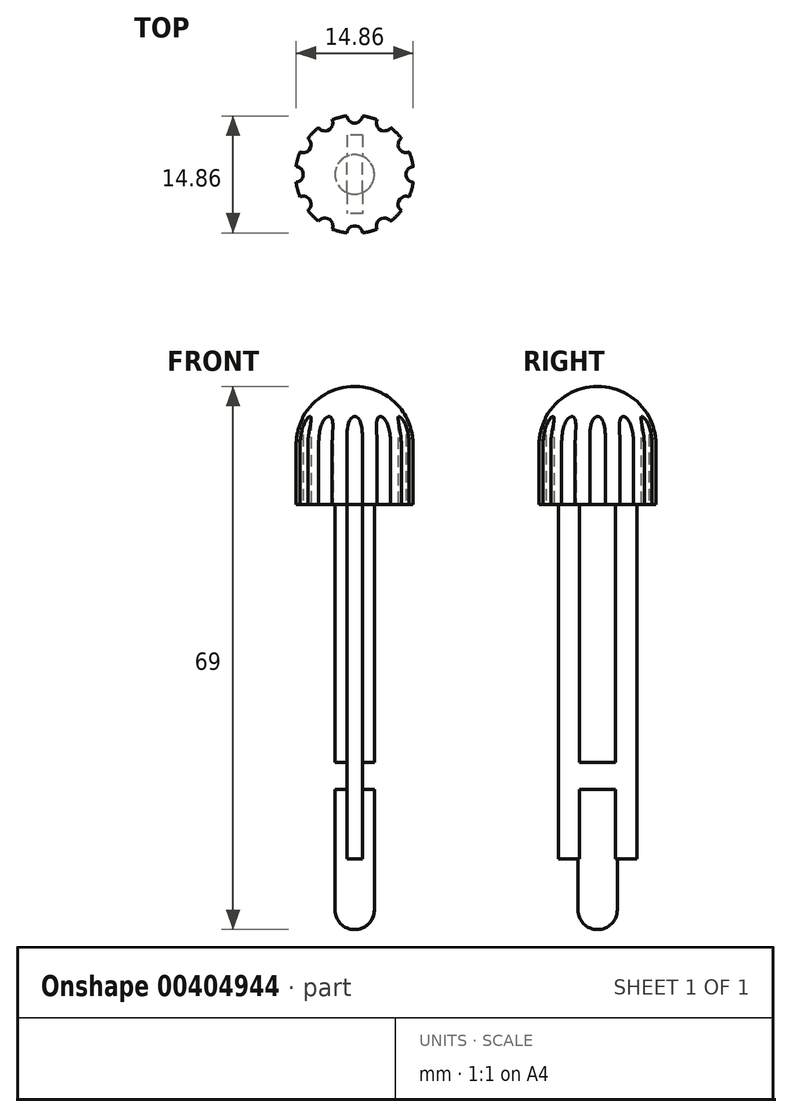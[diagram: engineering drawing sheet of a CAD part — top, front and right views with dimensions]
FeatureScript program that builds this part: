
annotation { "Feature Type Name" : "Feature", "Feature Type Description" : "" }
export const myFeature = defineFeature(function(context is Context, id is Id, definition is map)
    precondition{}
    {
        {
            var Q0;
            Q0=qCreatedBy(makeId("Top.planeOp"),FACE);
            var sketch = newSketch(context, id + "F0", { "sketchPlane" : qUnion([Q0])});
            skCircle(sketch, "E0", {"center": v(0, 0) * mm, "radius": 7.5 * mm});
            skCircle(sketch, "E1", {"center": v(0, 0) * mm, "radius": 2.5 * mm});
            skLineSegment(sketch, "E2.bottom", {"start": v(1, 5) * mm, "end": v(-1, 5) * mm});
            skLineSegment(sketch, "E2.top", {"start": v(1, -5) * mm, "end": v(-1, -5) * mm});
            skLineSegment(sketch, "E2.left", {"start": v(1, 5) * mm, "end": v(1, -5) * mm});
            skLineSegment(sketch, "E2.right", {"start": v(-1, 5) * mm, "end": v(-1, -5) * mm});
            skSolve(sketch);
        }
        {
            var Q0;
            Q0 = qSketchRegion(id + "F0", true);
            var Q1;
            {var subQ0=sQuery(id+"F0.wireOp",EDGE,"E2.left");var subQ1=sQuery(id+"F0.wireOp",EDGE,"E1");var subQ2=makeQuery(id+"F0.imprint","INTERSECT",VERTEX,{"disambiguationData":[OD(0.0)],"derivedFrom":[subQ1,subQ0]});Q1=makeQuery(id+"F0.imprint","IMPRINT",FACE,{"disambiguationData":[TD([[makeQuery(id+"F0.imprint","IMPRINT",EDGE,{"disambiguationData":[TD([[subQ2,1.0]])],"derivedFrom":subQ1}),1.0]])]});}
            var Q2;
            {var subQ0=sQuery(id+"F0.wireOp",EDGE,"E2.right");var subQ1=sQuery(id+"F0.wireOp",EDGE,"E1");var subQ2=makeQuery(id+"F0.imprint","INTERSECT",VERTEX,{"disambiguationData":[OD(0.0)],"derivedFrom":[subQ1,subQ0]});Q2=makeQuery(id+"F0.imprint","IMPRINT",FACE,{"disambiguationData":[TD([[makeQuery(id+"F0.imprint","IMPRINT",EDGE,{"disambiguationData":[TD([[subQ2,-1.0]])],"derivedFrom":subQ1}),1.0]])]});}
            var Q3;
            {var subQ0=sQuery(id+"F0.wireOp",EDGE,"E2.right");var subQ1=sQuery(id+"F0.wireOp",EDGE,"E1");var subQ2=makeQuery(id+"F0.imprint","INTERSECT",VERTEX,{"disambiguationData":[OD(0.0)],"derivedFrom":[subQ1,subQ0]});Q3=makeQuery(id+"F0.imprint","IMPRINT",FACE,{"disambiguationData":[TD([[makeQuery(id+"F0.imprint","IMPRINT",EDGE,{"disambiguationData":[TD([[subQ2,1.0]])],"derivedFrom":subQ1}),1.0]])]});}
            var Q4;
            {var subQ5=sQuery(id+"F0.wireOp",EDGE,"E2.bottom");Q4=makeQuery(id+"F0.imprint","IMPRINT",FACE,{"disambiguationData":[TD([[makeQuery(id+"F0.imprint","IMPRINT",EDGE,{"derivedFrom":subQ5}),1.0]])]});}
            var Q5;
            {var subQ5=sQuery(id+"F0.wireOp",EDGE,"E2.top");Q5=makeQuery(id+"F0.imprint","IMPRINT",FACE,{"disambiguationData":[TD([[makeQuery(id+"F0.imprint","IMPRINT",EDGE,{"derivedFrom":subQ5}),-1.0]])]});}
            extrude(context, id + "F1", {"entities" : qUnion([Q0, Q1, Q2, Q3, Q4, Q5]), "depth" : 15 * mm});
        }
        {
            var Q0;
            {var subQ0=sQuery(id+"F0.wireOp",EDGE,"E2.right");var subQ1=sQuery(id+"F0.wireOp",EDGE,"E1");var subQ2=makeQuery(id+"F0.imprint","INTERSECT",VERTEX,{"disambiguationData":[OD(0.0)],"derivedFrom":[subQ1,subQ0]});Q0=makeQuery(id+"F0.imprint","IMPRINT",FACE,{"disambiguationData":[TD([[makeQuery(id+"F0.imprint","IMPRINT",EDGE,{"disambiguationData":[TD([[subQ2,1.0]])],"derivedFrom":subQ1}),1.0]])]});}
            var Q1;
            {var subQ0=sQuery(id+"F0.wireOp",EDGE,"E2.right");var subQ1=sQuery(id+"F0.wireOp",EDGE,"E1");var subQ2=makeQuery(id+"F0.imprint","INTERSECT",VERTEX,{"disambiguationData":[OD(0.0)],"derivedFrom":[subQ1,subQ0]});Q1=makeQuery(id+"F0.imprint","IMPRINT",FACE,{"disambiguationData":[TD([[makeQuery(id+"F0.imprint","IMPRINT",EDGE,{"disambiguationData":[TD([[subQ2,-1.0]])],"derivedFrom":subQ1}),1.0]])]});}
            var Q2;
            {var subQ0=sQuery(id+"F0.wireOp",EDGE,"E2.left");var subQ1=sQuery(id+"F0.wireOp",EDGE,"E1");var subQ2=makeQuery(id+"F0.imprint","INTERSECT",VERTEX,{"disambiguationData":[OD(0.0)],"derivedFrom":[subQ1,subQ0]});Q2=makeQuery(id+"F0.imprint","IMPRINT",FACE,{"disambiguationData":[TD([[makeQuery(id+"F0.imprint","IMPRINT",EDGE,{"disambiguationData":[TD([[subQ2,1.0]])],"derivedFrom":subQ1}),1.0]])]});}
            extrude(context, id + "F2", {"entities" : qUnion([Q0, Q1, Q2]), "operationType" : NewBodyOperationType.ADD, "oppositeDirection" : true, "depth" : 54 * mm});
        }
        {
            var Q0;
            {var subQ5=sQuery(id+"F0.wireOp",EDGE,"E2.bottom");Q0=makeQuery(id+"F0.imprint","IMPRINT",FACE,{"disambiguationData":[TD([[makeQuery(id+"F0.imprint","IMPRINT",EDGE,{"derivedFrom":subQ5}),1.0]])]});}
            var Q1;
            {var subQ5=sQuery(id+"F0.wireOp",EDGE,"E2.top");Q1=makeQuery(id+"F0.imprint","IMPRINT",FACE,{"disambiguationData":[TD([[makeQuery(id+"F0.imprint","IMPRINT",EDGE,{"derivedFrom":subQ5}),-1.0]])]});}
            extrude(context, id + "F3", {"entities" : qUnion([Q0, Q1]), "operationType" : NewBodyOperationType.ADD, "oppositeDirection" : true, "depth" : 45 * mm});
        }
        {
            var Q0;
            Q0=makeQuery(id+"F2.opExtrude","CAP_FACE",FACE,{"disambiguationData":[OSD([sQuery(id+"F0.wireOp",EDGE,"E1")])],"isStart":false});
            fillet(context, id + "F4", {"entities" : qUnion([Q0]), "radius" : 2.5 * mm, "tangentPropagation" : true, "allowEdgeOverflow" : false});
        }
        {
            var Q0;
            Q0=makeQuery(id+"F1.opExtrude","CAP_FACE",FACE,{"disambiguationData":[OSD([sQuery(id+"F0.wireOp",EDGE,"E0")])],"isStart":false});
            fillet(context, id + "F5", {"entities" : qUnion([Q0]), "radius" : 7.5 * mm, "tangentPropagation" : true, "allowEdgeOverflow" : false});
        }
        {
            var Q0;
            Q0=makeQuery(id+"F3.opExtrude","SWEPT_FACE",FACE,{"disambiguationData":[OSD([sQuery(id+"F0.wireOp",EDGE,"E2.bottom")])]});
            var sketch = newSketch(context, id + "F6", { "sketchPlane" : qUnion([Q0])});
            skLineSegment(sketch, "E3.bottom", {"start": v(1, -32.74) * mm, "end": v(3.02, -32.74) * mm});
            skLineSegment(sketch, "E3.top", {"start": v(1, -36.22) * mm, "end": v(3.02, -36.22) * mm});
            skLineSegment(sketch, "E3.left", {"start": v(1, -32.74) * mm, "end": v(1, -36.22) * mm});
            skLineSegment(sketch, "E3.right", {"start": v(3.02, -32.74) * mm, "end": v(3.02, -36.22) * mm});
            skLineSegment(sketch, "E4.bottom", {"start": v(-1, -32.74) * mm, "end": v(-3.02, -32.74) * mm});
            skLineSegment(sketch, "E4.top", {"start": v(-1, -36.22) * mm, "end": v(-3.02, -36.22) * mm});
            skLineSegment(sketch, "E4.left", {"start": v(-1, -32.74) * mm, "end": v(-1, -36.22) * mm});
            skLineSegment(sketch, "E4.right", {"start": v(-3.02, -32.74) * mm, "end": v(-3.02, -36.22) * mm});
            skSolve(sketch);
        }
        {
            var Q0;
            Q0=makeQuery(id+"F6.imprint","IMPRINT",FACE,{"disambiguationData":[TD([[makeQuery(id+"F6.imprint","IMPRINT",EDGE,{"derivedFrom":sQuery(id+"F6.wireOp",EDGE,"E4.bottom")}),1.0]])]});
            var Q1;
            Q1=makeQuery(id+"F6.imprint","IMPRINT",FACE,{"disambiguationData":[TD([[makeQuery(id+"F6.imprint","IMPRINT",EDGE,{"derivedFrom":sQuery(id+"F6.wireOp",EDGE,"E3.bottom")}),-1.0]])]});
            extrude(context, id + "F7", {"entities" : qUnion([Q0, Q1]), "operationType" : NewBodyOperationType.REMOVE, "oppositeDirection" : true, "depth" : 25 * mm});
        }
        {
            var Q0;
            Q0=qCreatedBy(makeId("Top.planeOp"),FACE);
            var sketch = newSketch(context, id + "F8", { "sketchPlane" : qUnion([Q0])});
            skCircle(sketch, "E5", {"center": v(7.53, 0) * mm, "radius": 1 * mm});
            skCircle(sketch, "E6.1.0", {"center": v(6.52, -3.77) * mm, "radius": 1 * mm});
            skCircle(sketch, "E6.2.0", {"center": v(3.77, -6.52) * mm, "radius": 1 * mm});
            skCircle(sketch, "E6.3.0", {"center": v(0, -7.53) * mm, "radius": 1 * mm});
            skCircle(sketch, "E6.4.0", {"center": v(-3.77, -6.52) * mm, "radius": 1 * mm});
            skCircle(sketch, "E6.5.0", {"center": v(-6.52, -3.77) * mm, "radius": 1 * mm});
            skCircle(sketch, "E6.6.0", {"center": v(-7.53, 0) * mm, "radius": 1 * mm});
            skCircle(sketch, "E6.7.0", {"center": v(-6.52, 3.77) * mm, "radius": 1 * mm});
            skCircle(sketch, "E6.8.0", {"center": v(-3.77, 6.52) * mm, "radius": 1 * mm});
            skCircle(sketch, "E6.9.0", {"center": v(0, 7.53) * mm, "radius": 1 * mm});
            skCircle(sketch, "E6.10.0", {"center": v(3.77, 6.52) * mm, "radius": 1 * mm});
            skCircle(sketch, "E6.11.0", {"center": v(6.52, 3.77) * mm, "radius": 1 * mm});
            skPoint(sketch, "E6.center", {"position": v(0, 0) * mm});
            skLineSegment(sketch, "E6.anchor1", {"start": v(0, 0) * mm, "end": v(7.53, 0) * mm, "construction": true});
            skLineSegment(sketch, "E6.anchor2", {"start": v(0, 0) * mm, "end": v(6.52, 3.77) * mm, "construction": true});
            skSolve(sketch);
        }
        {
            var Q0;
            Q0=makeQuery(id+"F8.imprint","IMPRINT",FACE,{"disambiguationData":[TD([[makeQuery(id+"F8.imprint","IMPRINT",EDGE,{"derivedFrom":sQuery(id+"F8.wireOp",EDGE,"E6.5.0")}),1.0]])]});
            var Q1;
            Q1=makeQuery(id+"F8.imprint","IMPRINT",FACE,{"disambiguationData":[TD([[makeQuery(id+"F8.imprint","IMPRINT",EDGE,{"derivedFrom":sQuery(id+"F8.wireOp",EDGE,"E6.9.0")}),1.0]])]});
            var Q2;
            Q2=makeQuery(id+"F8.imprint","IMPRINT",FACE,{"disambiguationData":[TD([[makeQuery(id+"F8.imprint","IMPRINT",EDGE,{"derivedFrom":sQuery(id+"F8.wireOp",EDGE,"E6.1.0")}),1.0]])]});
            var Q3;
            Q3=makeQuery(id+"F8.imprint","IMPRINT",FACE,{"disambiguationData":[TD([[makeQuery(id+"F8.imprint","IMPRINT",EDGE,{"derivedFrom":sQuery(id+"F8.wireOp",EDGE,"E6.6.0")}),1.0]])]});
            var Q4;
            Q4=makeQuery(id+"F8.imprint","IMPRINT",FACE,{"disambiguationData":[TD([[makeQuery(id+"F8.imprint","IMPRINT",EDGE,{"derivedFrom":sQuery(id+"F8.wireOp",EDGE,"E6.11.0")}),1.0]])]});
            var Q5;
            Q5=makeQuery(id+"F8.imprint","IMPRINT",FACE,{"disambiguationData":[TD([[makeQuery(id+"F8.imprint","IMPRINT",EDGE,{"derivedFrom":sQuery(id+"F8.wireOp",EDGE,"E6.2.0")}),1.0]])]});
            var Q6;
            Q6=makeQuery(id+"F8.imprint","IMPRINT",FACE,{"disambiguationData":[TD([[makeQuery(id+"F8.imprint","IMPRINT",EDGE,{"derivedFrom":sQuery(id+"F8.wireOp",EDGE,"E6.3.0")}),1.0]])]});
            var Q7;
            Q7=makeQuery(id+"F8.imprint","IMPRINT",FACE,{"disambiguationData":[TD([[makeQuery(id+"F8.imprint","IMPRINT",EDGE,{"derivedFrom":sQuery(id+"F8.wireOp",EDGE,"E6.10.0")}),1.0]])]});
            var Q8;
            Q8=makeQuery(id+"F8.imprint","IMPRINT",FACE,{"disambiguationData":[TD([[makeQuery(id+"F8.imprint","IMPRINT",EDGE,{"derivedFrom":sQuery(id+"F8.wireOp",EDGE,"E6.7.0")}),1.0]])]});
            var Q9;
            Q9=makeQuery(id+"F8.imprint","IMPRINT",FACE,{"disambiguationData":[TD([[makeQuery(id+"F8.imprint","IMPRINT",EDGE,{"derivedFrom":sQuery(id+"F8.wireOp",EDGE,"E6.8.0")}),1.0]])]});
            var Q10;
            Q10=makeQuery(id+"F8.imprint","IMPRINT",FACE,{"disambiguationData":[TD([[makeQuery(id+"F8.imprint","IMPRINT",EDGE,{"derivedFrom":sQuery(id+"F8.wireOp",EDGE,"E5")}),1.0]])]});
            var Q11;
            Q11=makeQuery(id+"F8.imprint","IMPRINT",FACE,{"disambiguationData":[TD([[makeQuery(id+"F8.imprint","IMPRINT",EDGE,{"derivedFrom":sQuery(id+"F8.wireOp",EDGE,"E6.4.0")}),1.0]])]});
            extrude(context, id + "F9", {"entities" : qUnion([Q0, Q1, Q2, Q3, Q4, Q5, Q6, Q7, Q8, Q9, Q10, Q11]), "operationType" : NewBodyOperationType.REMOVE, "depth" : 21.1 * mm});
        }
    });
